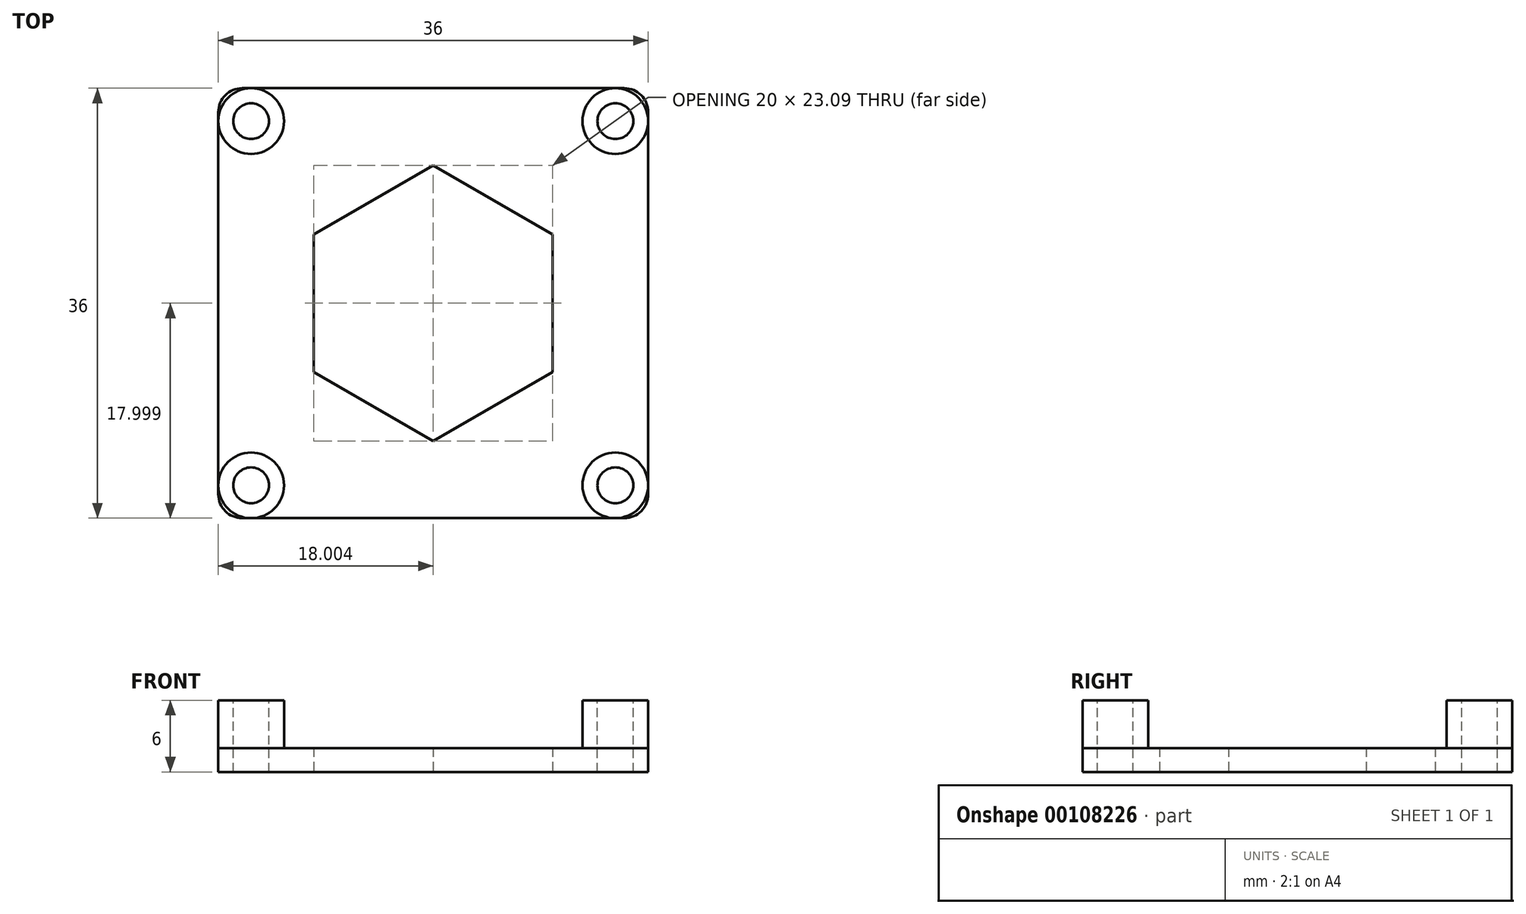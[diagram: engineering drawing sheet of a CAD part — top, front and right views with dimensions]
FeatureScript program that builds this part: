
annotation { "Feature Type Name" : "Feature", "Feature Type Description" : "" }
export const myFeature = defineFeature(function(context is Context, id is Id, definition is map)
    precondition{}
    {
        {
            var Q0;
            Q0=qCreatedBy(makeId("Top.planeOp"),FACE);
            var sketch = newSketch(context, id + "F0", { "sketchPlane" : qUnion([Q0])});
            skLineSegment(sketch, "E0.bottom", {"start": v(-40.66, 20.89) * mm, "end": v(-8.66, 20.89) * mm});
            skLineSegment(sketch, "E0.top", {"start": v(-40.66, -15.11) * mm, "end": v(-8.66, -15.11) * mm});
            skLineSegment(sketch, "E0.left", {"start": v(-42.66, 18.89) * mm, "end": v(-42.66, -13.11) * mm});
            skLineSegment(sketch, "E0.right", {"start": v(-6.66, 18.89) * mm, "end": v(-6.66, -13.11) * mm});
            skPoint(sketch, "E1.visualSharp", {"position": v(-42.66, 20.89) * mm});
            skArc(sketch, "E1.filletArc", {"start": v(-40.66, 20.89) * mm, "mid": v(-42.07, 20.3) * mm, "end": v(-42.66, 18.89) * mm});
            skPoint(sketch, "E2.visualSharp", {"position": v(-6.66, 20.89) * mm});
            skArc(sketch, "E2.filletArc", {"start": v(-6.66, 18.89) * mm, "mid": v(-7.24, 20.3) * mm, "end": v(-8.66, 20.89) * mm});
            skPoint(sketch, "E3.visualSharp", {"position": v(-6.66, -15.11) * mm});
            skArc(sketch, "E3.filletArc", {"start": v(-8.66, -15.11) * mm, "mid": v(-7.24, -14.53) * mm, "end": v(-6.66, -13.11) * mm});
            skPoint(sketch, "E4.visualSharp", {"position": v(-42.66, -15.11) * mm});
            skArc(sketch, "E4.filletArc", {"start": v(-42.66, -13.11) * mm, "mid": v(-42.07, -14.53) * mm, "end": v(-40.66, -15.11) * mm});
            skCircle(sketch, "E5.cCircle", {"center": v(-24.66, 2.89) * mm, "radius": 10 * mm, "construction": true});
            skLineSegment(sketch, "E5.0", {"start": v(-14.66, 8.66) * mm, "end": v(-14.66, -2.88) * mm});
            skLineSegment(sketch, "E5.1", {"start": v(-14.66, -2.88) * mm, "end": v(-24.66, -8.66) * mm});
            skLineSegment(sketch, "E5.2", {"start": v(-24.66, -8.66) * mm, "end": v(-34.66, -2.88) * mm});
            skLineSegment(sketch, "E5.3", {"start": v(-34.66, -2.88) * mm, "end": v(-34.66, 8.66) * mm});
            skLineSegment(sketch, "E5.4", {"start": v(-34.66, 8.66) * mm, "end": v(-24.66, 14.44) * mm});
            skLineSegment(sketch, "E5.5", {"start": v(-24.66, 14.44) * mm, "end": v(-14.66, 8.66) * mm});
            skPoint(sketch, "E5.0.midPoint", {"position": v(-14.66, 2.89) * mm});
            skSolve(sketch);
        }
        {
            var Q0;
            Q0=makeQuery(id+"F0.imprint","IMPRINT",FACE,{"disambiguationData":[TD([[makeQuery(id+"F0.imprint","IMPRINT",EDGE,{"derivedFrom":sQuery(id+"F0.wireOp",EDGE,"E0.bottom")}),-1.0]])]});
            extrude(context, id + "F1", {"entities" : qUnion([Q0]), "depth" : 2 * mm});
        }
        {
            var Q0;
            Q0=makeQuery(id+"F1.opExtrude","CAP_FACE",FACE,{"disambiguationData":[OSD([sQuery(id+"F0.wireOp",EDGE,"E0.bottom"),sQuery(id+"F0.wireOp",EDGE,"E0.top"),sQuery(id+"F0.wireOp",EDGE,"E0.left"),sQuery(id+"F0.wireOp",EDGE,"E0.right"),sQuery(id+"F0.wireOp",EDGE,"E1.filletArc"),sQuery(id+"F0.wireOp",EDGE,"E2.filletArc"),sQuery(id+"F0.wireOp",EDGE,"E3.filletArc"),sQuery(id+"F0.wireOp",EDGE,"E4.filletArc")])],"isStart":false});
            var sketch = newSketch(context, id + "F2", { "sketchPlane" : qUnion([Q0])});
            skCircle(sketch, "E6", {"center": v(-39.9, 18.14) * mm, "radius": 2.75 * mm});
            skCircle(sketch, "E7", {"center": v(-9.4, 18.14) * mm, "radius": 2.75 * mm});
            skCircle(sketch, "E8", {"center": v(-39.9, -12.36) * mm, "radius": 2.75 * mm});
            skCircle(sketch, "E9", {"center": v(-9.4, -12.36) * mm, "radius": 2.75 * mm});
            skSolve(sketch);
        }
        {
            var Q0;
            Q0=qSketchRegion(id+"F2",true);
            extrude(context, id + "F3", {"entities" : qUnion([Q0]), "operationType" : NewBodyOperationType.ADD, "depth" : 4 * mm});
        }
        {
            var Q0;
            Q0=makeQuery(id+"F3.opExtrude","CAP_FACE",FACE,{"disambiguationData":[OSD([sQuery(id+"F2.wireOp",EDGE,"E6")])],"isStart":false});
            var sketch = newSketch(context, id + "F4", { "sketchPlane" : qUnion([Q0])});
            skCircle(sketch, "E10", {"center": v(-39.9, 18.14) * mm, "radius": 1.5 * mm});
            skCircle(sketch, "E11", {"center": v(-9.4, 18.14) * mm, "radius": 1.5 * mm});
            skCircle(sketch, "E12", {"center": v(-9.4, -12.36) * mm, "radius": 1.5 * mm});
            skCircle(sketch, "E13", {"center": v(-39.9, -12.36) * mm, "radius": 1.5 * mm});
            skSolve(sketch);
        }
        {
            var Q0;
            Q0=qSketchRegion(id+"F4",true);
            extrude(context, id + "F5", {"entities" : qUnion([Q0]), "operationType" : NewBodyOperationType.REMOVE, "oppositeDirection" : true, "depth" : 25 * mm});
        }
    });
